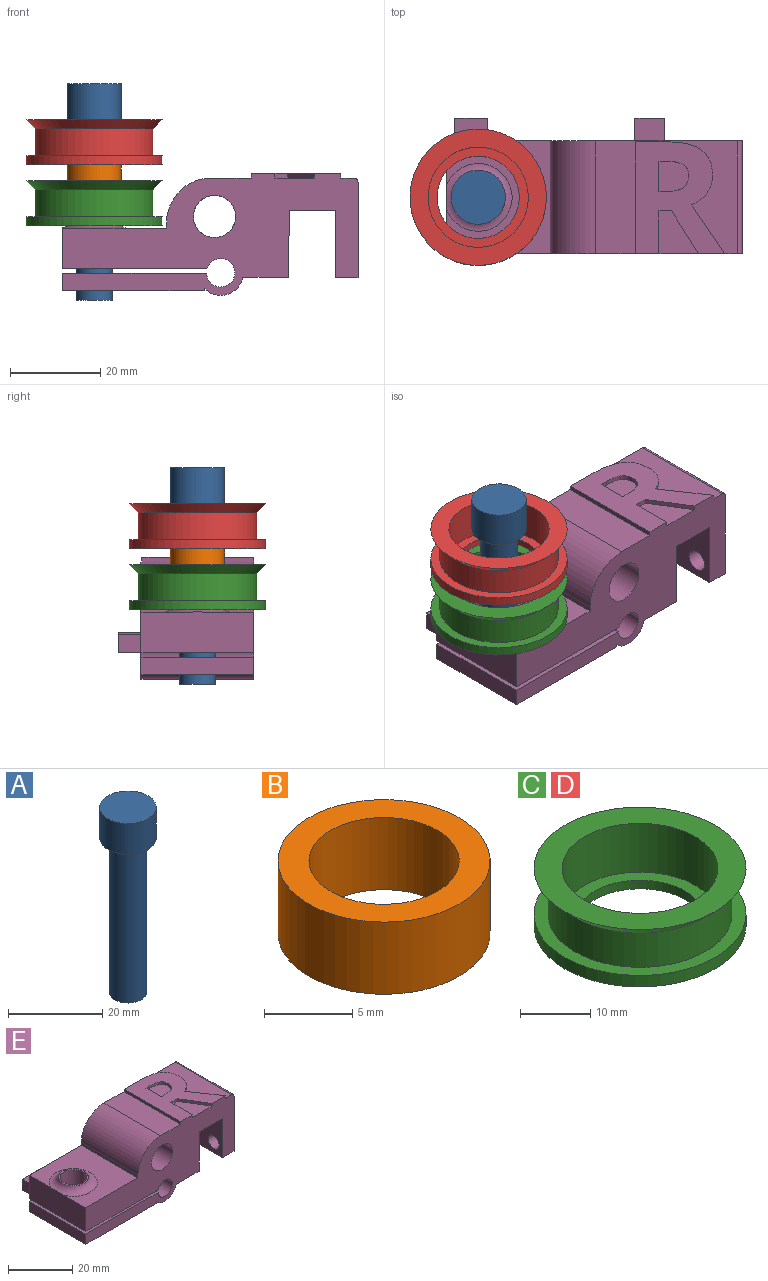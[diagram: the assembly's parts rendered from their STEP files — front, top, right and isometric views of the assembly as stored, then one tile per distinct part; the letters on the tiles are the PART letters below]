
ASSEMBLY  parts=5 mates=4
PART A: 5 faces, bbox 12x12x48 mm
  f0: cylinder r=4mm len=40mm, axis (0,0,-1), area 1005.3mm2, adj f1,f4
  f1: plane 8x8mm, normal (0,0,-1), area 50.3mm2, adj f0
  f2: cylinder r=6mm len=12mm, axis (0,0,-1), area 301.6mm2, adj f3,f4
  f3: plane 12x12mm, normal (0,0,1), area 113.1mm2, adj f2
  f4: plane 12x12mm, normal (0,0,-1), area 62.8mm2, adj f0,f2
PART B: 4 faces, bbox 12x12x5 mm
  f0: cylinder r=4.25mm len=8.5mm, axis (0,0,-1), area 133.5mm2, adj f2,f3
  f1: cylinder r=6mm len=12mm, axis (0,0,-1), area 188.5mm2, adj f2,f3
  f2: plane 12x12mm, normal (0,0,1), area 56.4mm2, adj f0,f1
  f3: plane 12x12mm, normal (0,0,-1), area 56.4mm2, adj f0,f1
PART C: 9 faces, bbox 30.2x30.2x10 mm
  f0: plane 30.2x30.2mm, normal (0,0,1), area 329.2mm2, adj f1,f8
  f1: cylinder r=11.1mm len=22.2mm, axis (0,0,-1), area 592.8mm2, adj f0,f2
  f2: plane 22.2x22.2mm, normal (0,0,1), area 126.9mm2, adj f1,f3
  f3: cylinder r=9.1mm len=18.2mm, axis (0,0,-1), area 85.8mm2, adj f2,f4
  f4: plane 30.2x30.2mm, normal (0,0,-1), area 456.2mm2, adj f3,f5
  f5: cylinder r=15.1mm len=30.2mm, axis (0,0,-1), area 189.8mm2, adj f4,f6
  f6: plane 30.2x30.2mm, normal (0,0,1), area 177.2mm2, adj f5,f7
  f7: cylinder r=13.1mm len=26.2mm, axis (0,0,-1), area 493.9mm2, adj f6,f8
  f8: cone r=15.1mm half-angle=45deg, axis (0,0,1), area 250.6mm2, adj f0,f7
PART D: same geometry as C
PART E: 57 faces, bbox 68.9x30x27 mm
  f0: plane 31.42x25mm, normal (0,0,1), area 392.1mm2, adj f15,f16,f26,f28,f41,f42,f43,f44
  f1: plane 9.51x8.71mm, normal (0,0,1), area 54.7mm2, adj f15,f38,f39,f40
  f2: plane 25x3.86mm, normal (-1,0,0), area 96.5mm2, adj f6,f15,f16,f20
  f3: cylinder r=4.17mm len=8.35mm, axis (0,0,1), area 101.3mm2, adj f6,f20
  f4: plane 25x10.1mm, normal (0,0,-1), area 252.6mm2, adj f14,f15,f16,f18
  f5: plane 25x0.6mm, normal (1,0,0), area 14.9mm2, adj f6,f15,f16,f18
  f6: plane 31.35x25mm, normal (0,0,-1), area 729mm2, adj f2,f3,f5,f15,f16
  f7: plane 25x9.08mm, normal (-1,0,0), area 226.1mm2, adj f8,f15,f16,f21,f25
  f8: plane 25x23mm, normal (0,0,1), area 400mm2, adj f7,f9,f15,f16,f25
  f9: plane 25x1.1mm, normal (-1,0,0), area 27.5mm2, adj f8,f15,f16,f26
  f10: plane 25x21.09mm, normal (1,0,0), area 493.5mm2, adj f11,f15,f16,f23,f24,f28
  f11: plane 25x5mm, normal (0,0,-1), area 125mm2, adj f10,f12,f15,f16
  f12: plane 25x15mm, normal (-1,0,0), area 341.3mm2, adj f11,f13,f15,f16,f23,f24
  f13: plane 25x10.2mm, normal (0,0,-1), area 255mm2, adj f12,f14,f15,f16
  f14: plane 25x14.91mm, normal (1,0,-0.01), area 372.8mm2, adj f4,f13,f15,f16
  f15: plane 65.42x27mm, normal (0,-1,0), area 1009.8mm2, adj f0,f1,f2,f4,f5,f6,f7,f8
  f16: plane 65.42x26mm, normal (0,1,0), area 938.8mm2, adj f0,f2,f4,f5,f6,f7,f8,f9
  f17: cylinder r=4.17mm len=11.04mm, axis (0,0,1), area 289.6mm2, adj f21,f22
  f18: cylinder r=5mm len=25mm, axis (0,-1,0), area 273.8mm2, adj f4,f5,f15,f16
  f19: cylinder r=3.15mm len=25mm, axis (0,-1,0), area 469.5mm2, adj f15,f16,f20,f21
  f20: plane 31.86x25mm, normal (0,0,1), area 741.8mm2, adj f2,f3,f15,f16,f19
  f21: plane 31.98x30mm, normal (0,0,-1), area 781.2mm2, adj f7,f15,f16,f17,f19,f30,f31,f32
  f22: plane 9.35x9.35mm, normal (0,0,1), area 13.9mm2, adj f17,f25
  f23: cylinder r=2.43mm len=5mm, axis (1,0,0), area 76.2mm2, adj f10,f12
  f24: cylinder r=2.2mm len=5mm, axis (1,0,0), area 69.1mm2, adj f10,f12
  f25: torus R=7.5mm, axis (0,0,-1), area 134.6mm2, adj f7,f8,f22
  f26: cylinder r=10mm len=25mm, axis (0,-1,0), area 392.7mm2, adj f0,f9,f15,f16
  f27: cylinder r=4.68mm len=25mm, axis (0,-1,0), area 735.2mm2, adj f15,f16
  f28: cylinder r=1mm len=25mm, axis (0,-1,0), area 39.3mm2, adj f0,f10,f15,f16
  f29: plane 7.3x5mm, normal (0,0,1), area 36.5mm2, adj f16,f30,f31,f32
  f30: plane 5x4.12mm, normal (-1,0,0), area 20.6mm2, adj f16,f21,f29,f32
  f31: plane 5x4.12mm, normal (1,0,0), area 20.6mm2, adj f16,f21,f29,f32
  f32: plane 7.3x4.12mm, normal (0,1,0), area 30.1mm2, adj f21,f29,f30,f31
  f33: plane 6.63x5mm, normal (0,0,1), area 33.2mm2, adj f16,f34,f36,f37
  f34: plane 5x4.5mm, normal (-1,0,0), area 22.5mm2, adj f16,f33,f35,f37
  f35: plane 6.63x5mm, normal (0,0,-1), area 33.2mm2, adj f16,f34,f36,f37
  f36: plane 5x4.5mm, normal (1,0,0), area 22.5mm2, adj f16,f33,f35,f37
  f37: plane 6.63x4.5mm, normal (0,1,0), area 29.9mm2, adj f33,f34,f35,f36
  f38: plane 9.51x1mm, normal (1,0,0), area 9.5mm2, adj f1,f15,f39,f55
  f39: plane 2.79x1mm, normal (0,-1,0), area 2.8mm2, adj f1,f38,f40,f55
  f40: plane 9.51x5.92mm, normal (-0.85,-0.53,0), area 11.2mm2, adj f1,f15,f39,f55
  f41: extruded ~10.8x7.29mm, area 13mm2, adj f0,f15,f42,f55
  f42: extruded ~3.41x2.67mm, area 4.4mm2, adj f0,f41,f43,f55
  f43: extruded ~3.89x1.2mm, area 4.1mm2, adj f0,f42,f44,f55
  f44: extruded ~5.59x2.42mm, area 6.3mm2, adj f0,f43,f45,f55
  f45: extruded ~7.48x1.84mm, area 7.8mm2, adj f0,f44,f46,f55
  f46: plane 7.22x1mm, normal (0,1,0), area 7.2mm2, adj f0,f45,f47,f55
  f47: plane 24.79x1mm, normal (-1,0,0), area 24.8mm2, adj f0,f15,f46,f55
  f48: plane 1.69x1mm, normal (0,1,0), area 1.7mm2, adj f49,f54,f55,f56
  f49: plane 6.7x1mm, normal (1,0,0), area 6.7mm2, adj f48,f50,f55,f56
  f50: plane 1.6x1mm, normal (0,-1,0), area 1.6mm2, adj f49,f51,f55,f56
  f51: extruded ~3.75x1mm, area 3.9mm2, adj f50,f52,f55,f56
  f52: extruded ~2.51x1.21mm, area 2.9mm2, adj f51,f53,f55,f56
  f53: extruded ~2.61x1.19mm, area 3mm2, adj f52,f54,f55,f56
  f54: extruded ~3.68x1mm, area 3.8mm2, adj f48,f53,f55,f56
  f55: plane 24.79x19.8mm, normal (0,0,1), area 300mm2, adj f15,f38,f39,f40,f41,f42,f43,f44
  f56: plane 6.7x6.56mm, normal (0,0,1), area 38.8mm2, adj f48,f49,f50,f51,f52,f53,f54
PLACE A t=(-103.78,-12.5,-5.1)mm
PLACE B rot(axis=(1,0,0),180deg) t=(-103.78,-12.5,24.9)mm
PLACE C t=(-103.78,-12.5,16.6)mm
PLACE D t=(-103.78,-12.5,30.1)mm
PLACE E at identity
MATE fastened A.f0 <-> D.f1  axis (0,0,-1) through (-103.78,-12.5,34.9)mm
MATE fastened B.f0 <-> C.f1  axis (0,0,1) through (-103.78,-12.5,19.9)mm
MATE fastened C.f1 <-> E.f3  axis (0,0,-1) through (-103.78,-12.5,11.4)mm
MATE fastened D.f1 <-> B.f0  axis (0,0,-1) through (-103.78,-12.5,24.9)mm
